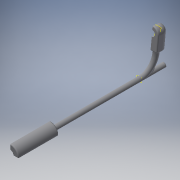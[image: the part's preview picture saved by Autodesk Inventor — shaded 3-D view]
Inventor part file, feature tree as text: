
AUTODESK INVENTOR PART (.ipt)
format: ipt  version: 2018 (Build 220112000, 112)  size: 485,376 bytes
history: native  units: mm
features: sketch x10, extrude x8, fillet x5, projected_geometry x3, plane x2, revolve x1, sweep x1, mirror x1
ambient origin geometry x8: Origin, YZ Plane, XZ Plane, XY Plane, X Axis, Y Axis, Z Axis, Center Point
bodies: Solid1 (feature_tree)
feature tree (31):
  revolve  "Revolution1"  [1 undecoded]
  fillet  "Fillet1"  Radius=8.0mm
  fillet  "Fillet2"  Radius=40.0mm
  fillet  "Fillet3"  [1 undecoded]
  plane  "Work Plane1"
  sweep  "Sweep1"
  extrude  "Extrusion2"  Depth=1.5mm
  fillet  "Fillet4"  Radius=1.0mm
  fillet  "Fillet5"  Radius=1.0mm
  extrude  "Extrusion3"  Depth=1.0mm
  extrude  "Extrusion4"  Depth=6.601018mm
  extrude  "Extrusion5"  Depth=1.0mm
  extrude  "Extrusion6"  [1 undecoded]
  extrude  "Extrusion7"  Depth=18.0mm
  plane  "Work Plane3"
  extrude  "Extrusion8"  TaperAngle=0.0deg  [1 undecoded]
  extrude  "Extrusion9"  Depth=10.0mm
  mirror  "Mirror1"
  sketch  "Sketch6"  dims[d0=150.0mm d1=3.0mm d3=8.0mm d4=40.0mm d5=90.0deg]
  sketch  "Sketch8"  dims[d20=1.5mm d21=1.5mm]
  sketch  "Sketch9"  dims[d22=1.5mm d23=1.0mm d24=1.0mm d25=1.0mm]
  projected_geometry  "Projected Loop3"
  sketch  "Sketch10"  dims[d26=1.0mm d27=1.0mm]
  projected_geometry  "Projected Loop4"
  sketch  "Sketch11"  dims[d28=1.456552mm d29=6.601018mm]
  sketch  "Sketch12"  dims[d30=2.0mm d31=1.0mm]
  sketch  "Sketch13"  dims[d32=1.0mm d33=-23.0mm]
  sketch  "Sketch14"  dims[d38=18.0mm d39=18.0mm]
  sketch  "Sketch15"  dims[d40=16.0mm d41=0.0mm d42=0.0mm]
  projected_geometry  "Projected Loop5"
  sketch  "Sketch16"  dims[d43=12.0mm d44=5.0mm d45=6.0mm d46=6.0mm d47=20.0mm d48=0.0mm d49=6.0mm d50=1.0mm d51=3.0mm d52=5.5mm d53=8.0mm d54=0.0mm d55=10.0mm d56=0.0mm d57=50.0mm d58=0.0mm d59=1.4mm d60=0.0mm d61=4.332171mm d62=15.0mm d63=0.0mm d64=-3.0mm d65=6.5mm d66=1.1mm d67=0.0mm d68=10.0mm d69=0.0mm]
note: 4 required parameter values undecoded (feature->parameter linkage not recoverable at this tier; creation-order binding heuristic only, values carry confidence <= 0.55)